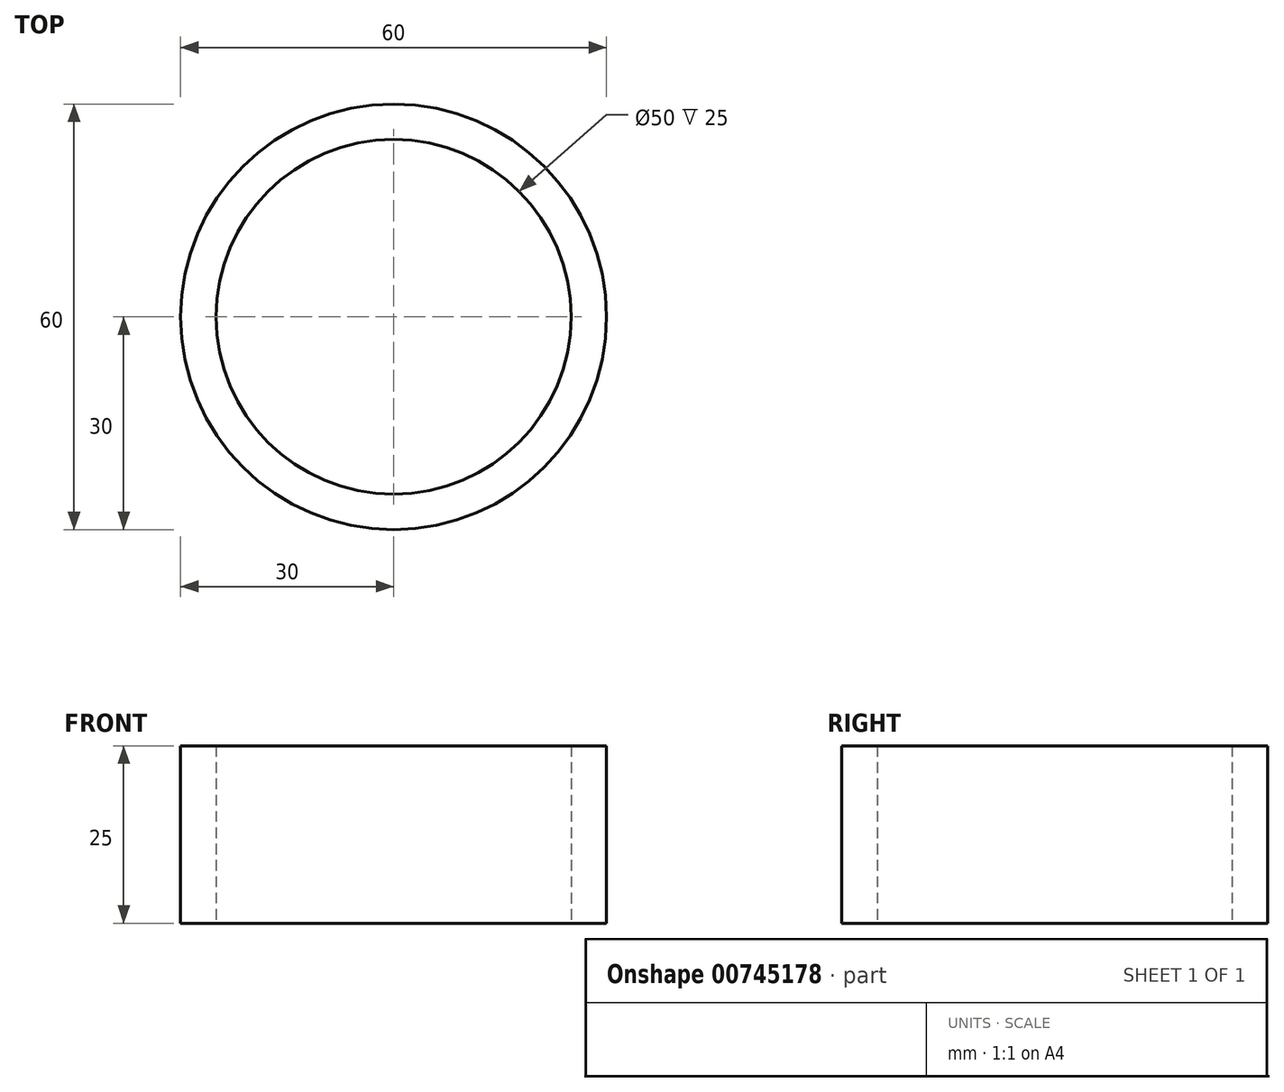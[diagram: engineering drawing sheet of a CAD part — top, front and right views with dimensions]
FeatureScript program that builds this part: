
annotation { "Feature Type Name" : "Feature", "Feature Type Description" : "" }
export const myFeature = defineFeature(function(context is Context, id is Id, definition is map)
    precondition{}
    {
        {
            var Q0;
            Q0=qCreatedBy(makeId("Top.planeOp"),FACE);
            var sketch = newSketch(context, id + "F0", { "sketchPlane" : qUnion([Q0])});
            skCircle(sketch, "E0", {"center": v(0, 0) * mm, "radius": 30 * mm});
            skCircle(sketch, "E1", {"center": v(0, 0) * mm, "radius": 25 * mm});
            skSolve(sketch);
        }
        {
            var Q0;
            Q0 = qSketchRegion(id + "F0", true);
            extrude(context, id + "F1", {"entities" : qUnion([Q0]), "depth" : 25 * mm, "offsetDistance" : 25 * mm});
        }
    });
